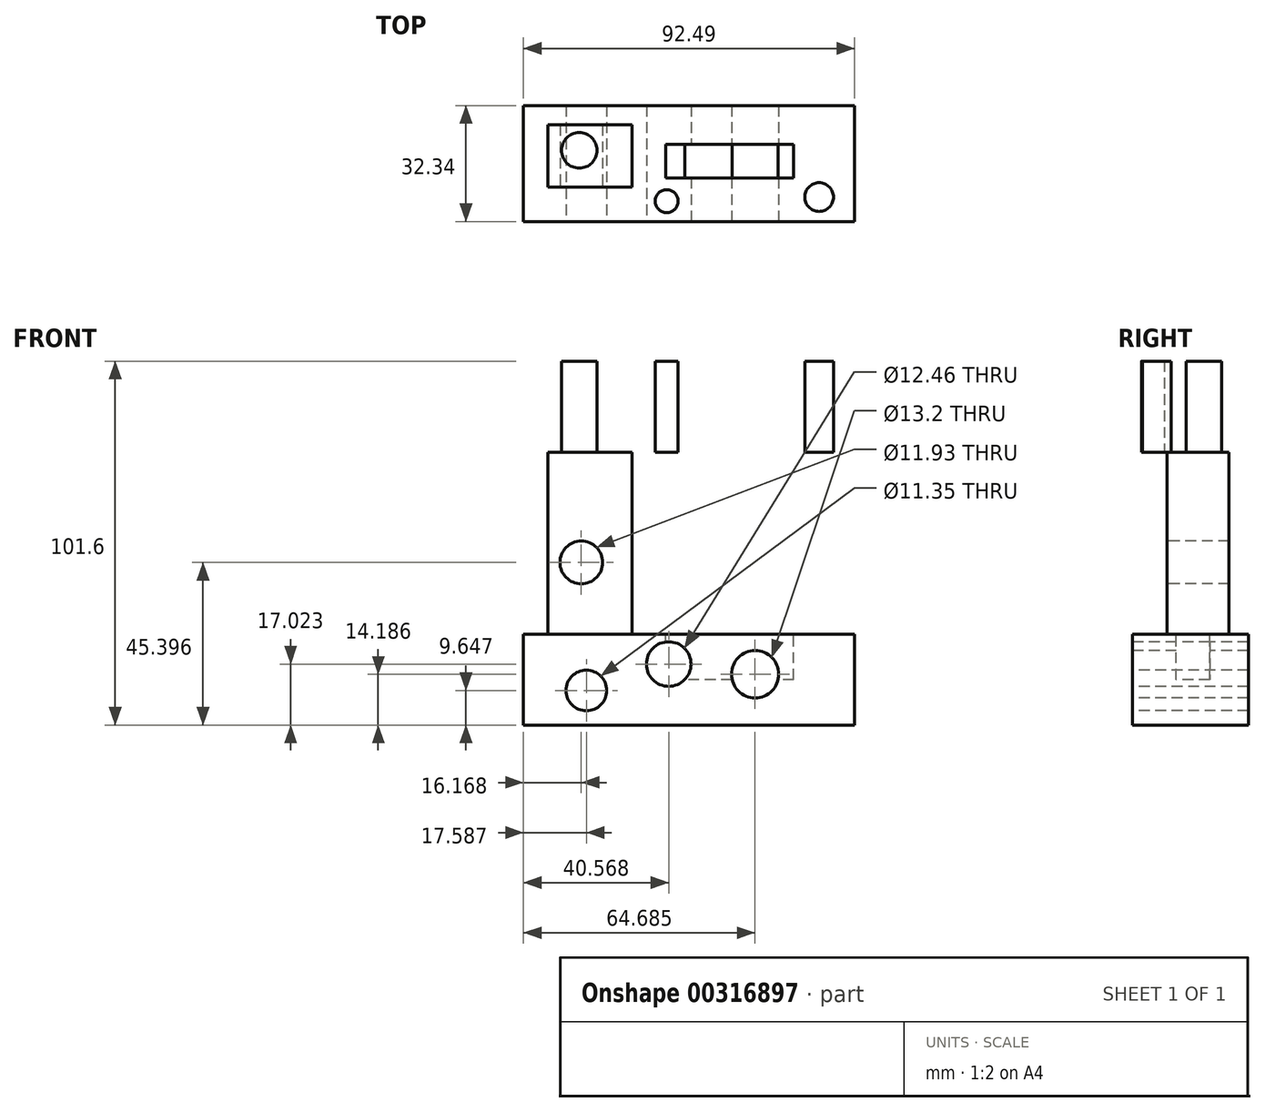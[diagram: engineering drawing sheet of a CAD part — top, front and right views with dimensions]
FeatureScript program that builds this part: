
annotation { "Feature Type Name" : "Feature", "Feature Type Description" : "" }
export const myFeature = defineFeature(function(context is Context, id is Id, definition is map)
    precondition{}
    {
        {
            var Q0;
            Q0=qCreatedBy(makeId("Top.planeOp"),FACE);
            var sketch = newSketch(context, id + "F0", { "sketchPlane" : qUnion([Q0])});
            skLineSegment(sketch, "E0", {"start": v(43.4, 44.54) * mm, "end": v(-49.08, 44.54) * mm});
            skLineSegment(sketch, "E1", {"start": v(-49.08, 44.54) * mm, "end": v(-49.08, 12.2) * mm});
            skLineSegment(sketch, "E2", {"start": v(-49.08, 12.2) * mm, "end": v(43.4, 12.2) * mm});
            skLineSegment(sketch, "E3", {"start": v(43.4, 12.2) * mm, "end": v(43.4, 44.54) * mm});
            skSolve(sketch);
        }
        {
            var Q0;
            Q0=makeQuery(id+"F0.imprint","IMPRINT",FACE,{"disambiguationData":[TD([[makeQuery(id+"F0.imprint","IMPRINT",EDGE,{"derivedFrom":sQuery(id+"F0.wireOp",EDGE,"E0")}),1.0]])]});
            extrude(context, id + "F1", {"entities" : qUnion([Q0]), "depth" : 25.4 * mm});
        }
        {
            var Q0;
            Q0=makeQuery(id+"F1.opExtrude","CAP_FACE",FACE,{"disambiguationData":[OSD([sQuery(id+"F0.wireOp",EDGE,"E0"),sQuery(id+"F0.wireOp",EDGE,"E1"),sQuery(id+"F0.wireOp",EDGE,"E2"),sQuery(id+"F0.wireOp",EDGE,"E3")])],"isStart":false});
            var sketch = newSketch(context, id + "F2", { "sketchPlane" : qUnion([Q0])});
            skLineSegment(sketch, "E4", {"start": v(-18.73, 39.15) * mm, "end": v(-42.27, 39.15) * mm});
            skLineSegment(sketch, "E5", {"start": v(-42.27, 39.15) * mm, "end": v(-42.27, 21.85) * mm});
            skLineSegment(sketch, "E6", {"start": v(-42.27, 21.85) * mm, "end": v(-18.73, 21.85) * mm});
            skLineSegment(sketch, "E7", {"start": v(-18.73, 21.85) * mm, "end": v(-18.73, 39.15) * mm});
            skSolve(sketch);
        }
        {
            var Q0;
            Q0=makeQuery(id+"F2.imprint","IMPRINT",FACE,{"disambiguationData":[TD([[makeQuery(id+"F2.imprint","IMPRINT",EDGE,{"derivedFrom":sQuery(id+"F2.wireOp",EDGE,"E4")}),1.0]])]});
            extrude(context, id + "F3", {"entities" : qUnion([Q0]), "operationType" : NewBodyOperationType.ADD, "depth" : 25.4 * mm});
        }
        {
            var Q0;
            Q0=makeQuery(id+"F3.opExtrude","CAP_FACE",FACE,{"disambiguationData":[OSD([sQuery(id+"F2.wireOp",EDGE,"E4"),sQuery(id+"F2.wireOp",EDGE,"E5"),sQuery(id+"F2.wireOp",EDGE,"E6"),sQuery(id+"F2.wireOp",EDGE,"E7")])],"isStart":false});
            extrude(context, id + "F4", {"entities" : qUnion([Q0]), "operationType" : NewBodyOperationType.ADD, "depth" : 25.4 * mm});
        }
        {
            var Q0;
            Q0=makeQuery(id+"F1.opExtrude","CAP_FACE",FACE,{"disambiguationData":[OSD([sQuery(id+"F0.wireOp",EDGE,"E0"),sQuery(id+"F0.wireOp",EDGE,"E1"),sQuery(id+"F0.wireOp",EDGE,"E2"),sQuery(id+"F0.wireOp",EDGE,"E3")])],"isStart":false});
            var sketch = newSketch(context, id + "F5", { "sketchPlane" : qUnion([Q0])});
            skLineSegment(sketch, "E8", {"start": v(26.39, 33.76) * mm, "end": v(-9.36, 33.76) * mm});
            skLineSegment(sketch, "E9", {"start": v(-9.36, 33.76) * mm, "end": v(-9.36, 24.4) * mm});
            skLineSegment(sketch, "E10", {"start": v(-9.36, 24.4) * mm, "end": v(26.39, 24.4) * mm});
            skLineSegment(sketch, "E11", {"start": v(26.39, 24.4) * mm, "end": v(26.39, 33.76) * mm});
            skSolve(sketch);
        }
        {
            var Q0;
            Q0=makeQuery(id+"F5.imprint","IMPRINT",FACE,{"disambiguationData":[TD([[makeQuery(id+"F5.imprint","IMPRINT",EDGE,{"derivedFrom":sQuery(id+"F5.wireOp",EDGE,"E8")}),1.0]])]});
            extrude(context, id + "F6", {"entities" : qUnion([Q0]), "operationType" : NewBodyOperationType.REMOVE, "oppositeDirection" : true, "depth" : 12.7 * mm});
        }
        {
            var Q0;
            Q0=makeQuery(id+"F1.opExtrude","SWEPT_FACE",FACE,{"disambiguationData":[OSD([sQuery(id+"F0.wireOp",EDGE,"E2")])]});
            var sketch = newSketch(context, id + "F7", { "sketchPlane" : qUnion([Q0])});
            skCircle(sketch, "E12", {"center": v(-8.51, 17.02) * mm, "radius": 6.23 * mm});
            skSolve(sketch);
        }
        {
            var Q0;
            Q0=makeQuery(id+"F7.imprint","IMPRINT",FACE,{"disambiguationData":[TD([[makeQuery(id+"F7.imprint","IMPRINT",EDGE,{"derivedFrom":sQuery(id+"F7.wireOp",EDGE,"E12")}),1.0]])]});
            extrude(context, id + "F8", {"entities" : qUnion([Q0]), "operationType" : NewBodyOperationType.REMOVE, "endBound" : BoundingType.THROUGH_ALL, "oppositeDirection" : true, "depth" : 25.4 * mm});
        }
        {
            var Q0;
            Q0=makeQuery(id+"F1.opExtrude","SWEPT_FACE",FACE,{"disambiguationData":[OSD([sQuery(id+"F0.wireOp",EDGE,"E2")])]});
            var sketch = newSketch(context, id + "F9", { "sketchPlane" : qUnion([Q0])});
            skCircle(sketch, "E13", {"center": v(15.6, 14.19) * mm, "radius": 6.6 * mm});
            skCircle(sketch, "E14", {"center": v(-31.5, 9.65) * mm, "radius": 5.67 * mm});
            skCircle(sketch, "E15", {"center": v(-32.91, 45.4) * mm, "radius": 5.96 * mm});
            skSolve(sketch);
        }
        {
            var Q0;
            Q0=makeQuery(id+"F9.imprint","IMPRINT",FACE,{"disambiguationData":[TD([[makeQuery(id+"F9.imprint","IMPRINT",EDGE,{"derivedFrom":sQuery(id+"F9.wireOp",EDGE,"E15")}),1.0]])]});
            var Q1;
            Q1=makeQuery(id+"F9.imprint","IMPRINT",FACE,{"disambiguationData":[TD([[makeQuery(id+"F9.imprint","IMPRINT",EDGE,{"derivedFrom":sQuery(id+"F9.wireOp",EDGE,"E14")}),1.0]])]});
            var Q2;
            Q2=makeQuery(id+"F9.imprint","IMPRINT",FACE,{"disambiguationData":[TD([[makeQuery(id+"F9.imprint","IMPRINT",EDGE,{"derivedFrom":sQuery(id+"F9.wireOp",EDGE,"E13")}),1.0]])]});
            extrude(context, id + "F10", {"entities" : qUnion([Q0, Q1, Q2]), "operationType" : NewBodyOperationType.REMOVE, "endBound" : BoundingType.THROUGH_ALL, "oppositeDirection" : true, "depth" : 25.4 * mm});
        }
        {
            var Q0;
            Q0=makeQuery(id+"F4.opExtrude","CAP_FACE",FACE,{"disambiguationData":[OSD([sQuery(id+"F2.wireOp",EDGE,"E4"),sQuery(id+"F2.wireOp",EDGE,"E5"),sQuery(id+"F2.wireOp",EDGE,"E6"),sQuery(id+"F2.wireOp",EDGE,"E7")])],"isStart":false});
            var sketch = newSketch(context, id + "F11", { "sketchPlane" : qUnion([Q0])});
            skCircle(sketch, "E16", {"center": v(-33.48, 32.06) * mm, "radius": 4.96 * mm});
            skCircle(sketch, "E17", {"center": v(33.48, 19) * mm, "radius": 4.01 * mm});
            skCircle(sketch, "E18", {"center": v(-9.08, 17.87) * mm, "radius": 3.2 * mm});
            skSolve(sketch);
        }
        {
            var Q0;
            Q0=makeQuery(id+"F11.imprint","IMPRINT",FACE,{"disambiguationData":[TD([[makeQuery(id+"F11.imprint","IMPRINT",EDGE,{"derivedFrom":sQuery(id+"F11.wireOp",EDGE,"E16")}),1.0]])]});
            var Q1;
            Q1=makeQuery(id+"F11.imprint","IMPRINT",FACE,{"disambiguationData":[TD([[makeQuery(id+"F11.imprint","IMPRINT",EDGE,{"derivedFrom":sQuery(id+"F11.wireOp",EDGE,"E18")}),1.0]])]});
            var Q2;
            Q2=makeQuery(id+"F11.imprint","IMPRINT",FACE,{"disambiguationData":[TD([[makeQuery(id+"F11.imprint","IMPRINT",EDGE,{"derivedFrom":sQuery(id+"F11.wireOp",EDGE,"E17")}),1.0]])]});
            extrude(context, id + "F12", {"entities" : qUnion([Q0, Q1, Q2]), "operationType" : NewBodyOperationType.ADD, "depth" : 25.4 * mm});
        }
    });
